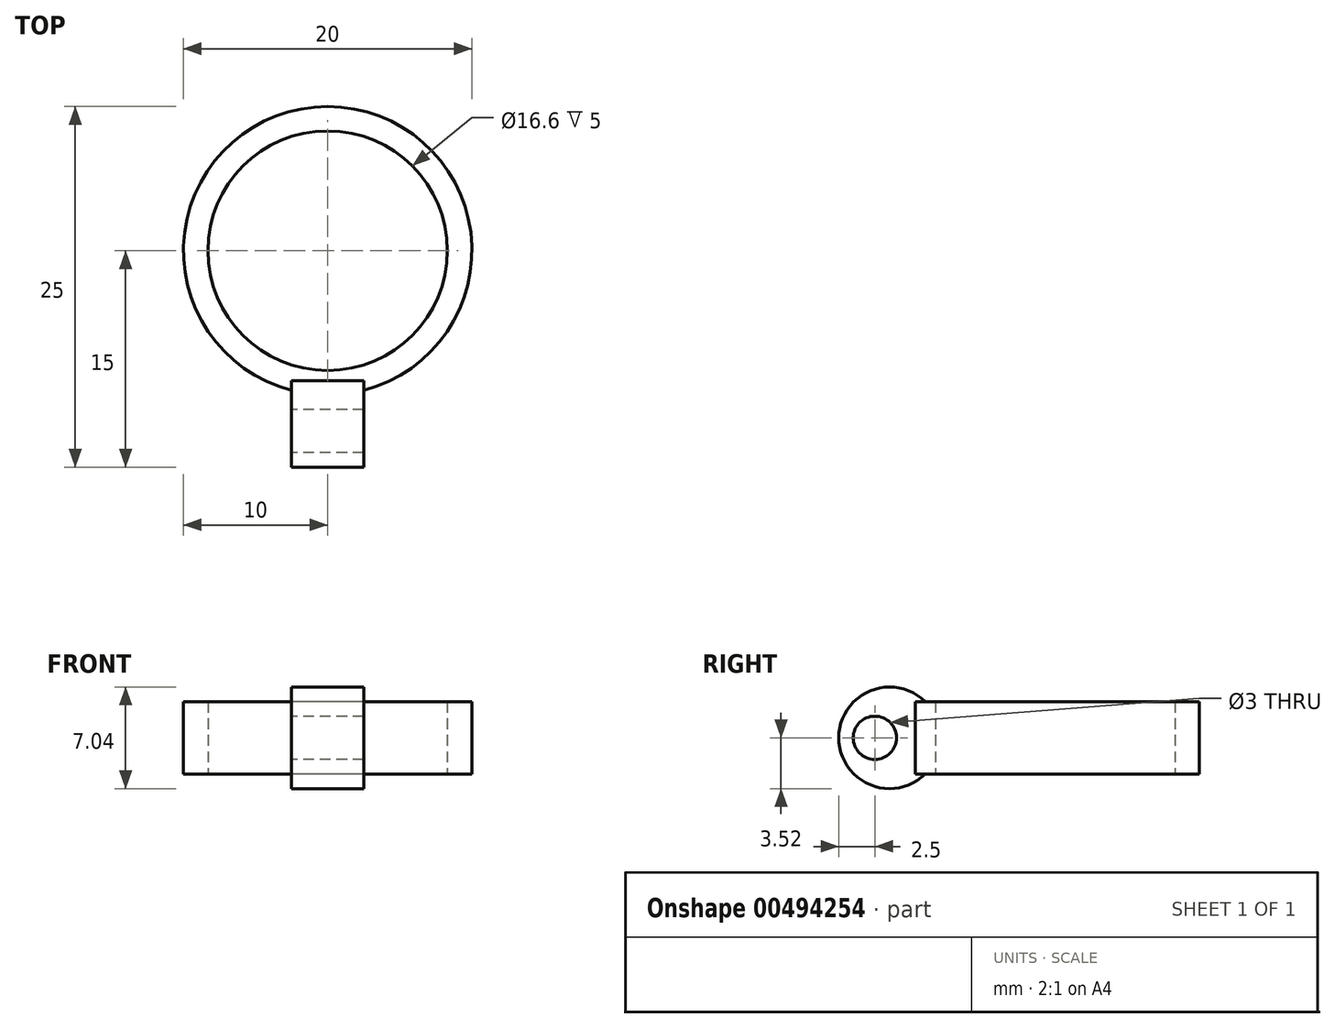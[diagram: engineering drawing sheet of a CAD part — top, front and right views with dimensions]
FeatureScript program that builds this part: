
annotation { "Feature Type Name" : "Feature", "Feature Type Description" : "" }
export const myFeature = defineFeature(function(context is Context, id is Id, definition is map)
    precondition{}
    {
        {
            var Q0;
            Q0=qCreatedBy(makeId("Top.planeOp"),FACE);
            var sketch = newSketch(context, id + "F0", { "sketchPlane" : qUnion([Q0])});
            skCircle(sketch, "E0", {"center": v(0, 0) * mm, "radius": 8.3 * mm});
            skCircle(sketch, "E1", {"center": v(0, 0) * mm, "radius": 10 * mm});
            skPoint(sketch, "E2", {"position": v(0, -10) * mm});
            skSolve(sketch);
        }
        {
            var Q0;
            Q0=makeQuery(id+"F0.imprint","IMPRINT",FACE,{"disambiguationData":[TD([[makeQuery(id+"F0.imprint","IMPRINT",EDGE,{"derivedFrom":sQuery(id+"F0.wireOp",EDGE,"E0")}),-1.0]])]});
            extrude(context, id + "F1", {"entities" : qUnion([Q0]), "depth" : 5 * mm, "offsetDistance" : 25 * mm});
        }
        {
            var Q0;
            Q0=qCreatedBy(makeId("Right.planeOp"),FACE);
            var sketch = newSketch(context, id + "F2", { "sketchPlane" : qUnion([Q0])});
            skLineSegment(sketch, "E3", {"start": v(0, 0) * mm, "end": v(0, 2.5) * mm, "construction": true});
            skLineSegment(sketch, "E4", {"start": v(0, 2.5) * mm, "end": v(-10, 2.5) * mm, "construction": true});
            skLineSegment(sketch, "E5", {"start": v(-10, 2.5) * mm, "end": v(-15, 2.5) * mm, "construction": true});
            skCircle(sketch, "E6", {"center": v(-12.5, 2.5) * mm, "radius": 1.5 * mm});
            skLineSegment(sketch, "E7", {"start": v(0, 2.5) * mm, "end": v(0, 5) * mm, "construction": true});
            skLineSegment(sketch, "E8", {"start": v(0, 5) * mm, "end": v(-9, 5) * mm, "construction": true});
            skLineSegment(sketch, "E9", {"start": v(-9, 5) * mm, "end": v(-14, 5) * mm, "construction": true});
            skLineSegment(sketch, "E10", {"start": v(0, 0) * mm, "end": v(-9, 0) * mm, "construction": true});
            skLineSegment(sketch, "E11", {"start": v(-9, 0) * mm, "end": v(-14, 0) * mm, "construction": true});
            skArc(sketch, "E12", {"start": v(-9, 5) * mm, "mid": v(-15, 2.5) * mm, "end": v(-9, 0) * mm});
            skLineSegment(sketch, "E13", {"start": v(-9, 5) * mm, "end": v(-9, 0) * mm});
            skSolve(sketch);
        }
        {
            var Q0;
            Q0=makeQuery(id+"F2.imprint","IMPRINT",FACE,{"disambiguationData":[TD([[makeQuery(id+"F2.imprint","IMPRINT",EDGE,{"derivedFrom":sQuery(id+"F2.wireOp",EDGE,"E6")}),-1.0]])]});
            extrude(context, id + "F3", {"entities" : qUnion([Q0]), "operationType" : NewBodyOperationType.ADD, "depth" : 5 * mm, "offsetDistance" : 25 * mm, "symmetric" : true});
        }
    });
